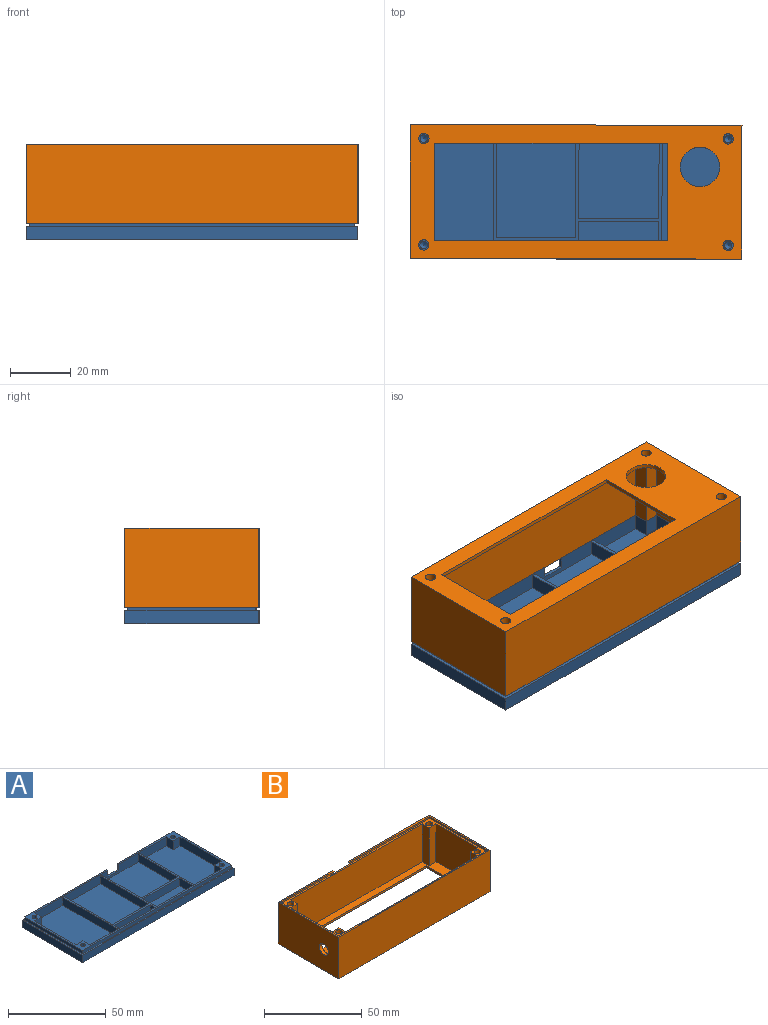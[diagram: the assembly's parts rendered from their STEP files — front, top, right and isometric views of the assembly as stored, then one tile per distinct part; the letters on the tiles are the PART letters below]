
ASSEMBLY  parts=2 mates=1
PART A: 58 faces, bbox 109x44x6.5 mm
  f0: plane 107x5mm, normal (0,1,0), area 218.5mm2, adj f27,f28,f30,f31,f40,f41,f50,f55
  f1: plane 35x26mm, normal (0,0,1), area 910mm2, adj f19,f20,f21,f25
  f2: plane 28.75x26.3mm, normal (0,0,1), area 756.1mm2, adj f16,f17,f18,f25
  f3: plane 40x24.2mm, normal (0,0,1), area 919.2mm2, adj f15,f24,f25,f26,f32,f33,f34,f35
  f4: plane 26.3x10.25mm, normal (0,0,1), area 269.6mm2, adj f12,f13,f14,f26
  f5: plane 26x4mm, normal (0,0,1), area 104mm2, adj f9,f10,f11,f26
  f6: plane 40x25.5mm, normal (0,0,1), area 970mm2, adj f8,f23,f25,f26,f36,f37,f38,f39
  f7: plane 109x44mm, normal (0,0,-1), area 4796mm2, adj f51,f52,f53,f54
  f8: plane 40x5mm, normal (-1,0,0), area 200mm2, adj f6,f22,f25,f26
  f9: plane 5x4mm, normal (1,0,0), area 20mm2, adj f5,f10,f22,f26
  f10: plane 26x5mm, normal (0,-1,0), area 130mm2, adj f5,f9,f11,f22
  f11: plane 5x4mm, normal (-1,0,0), area 20mm2, adj f5,f10,f22,f26
  f12: plane 10.25x5mm, normal (1,0,0), area 51.3mm2, adj f4,f13,f22,f26
  f13: plane 26.3x5mm, normal (0,-1,0), area 131.5mm2, adj f4,f12,f14,f22
  f14: plane 10.25x5mm, normal (-1,0,0), area 51.3mm2, adj f4,f13,f22,f26
  f15: plane 40x5mm, normal (1,0,0), area 200mm2, adj f3,f22,f25,f26
  f16: plane 28.75x5mm, normal (-1,0,0), area 143.8mm2, adj f2,f17,f22,f25
  f17: plane 26.3x5mm, normal (0,1,0), area 131.5mm2, adj f2,f16,f18,f22
  f18: plane 28.75x5mm, normal (1,0,0), area 143.8mm2, adj f2,f17,f22,f25
  f19: plane 35x5mm, normal (-1,0,0), area 175mm2, adj f1,f20,f22,f25
  f20: plane 26x5mm, normal (0,1,0), area 130mm2, adj f1,f19,f21,f22
  f21: plane 35x5mm, normal (1,0,0), area 175mm2, adj f1,f20,f22,f25
  f22: plane 55.3x40mm, normal (0,0,1), area 172.3mm2, adj f8,f9,f10,f11,f12,f13,f14,f15
  f23: plane 30x5.5mm, normal (1,0,0), area 165mm2, adj f6,f37,f38,f40
  f24: plane 30x5.5mm, normal (-1,0,0), area 165mm2, adj f3,f33,f34,f40
  f25: plane 95.12x5.5mm, normal (0,-1,0), area 478.1mm2, adj f1,f2,f3,f6,f8,f15,f16,f18
  f26: plane 95.12x5.5mm, normal (0,1,0), area 508.1mm2, adj f3,f4,f5,f6,f8,f9,f11,f12
  f27: plane 3.9x1mm, normal (1,0,0), area 3.9mm2, adj f0,f25,f40,f41
  f28: plane 42x2mm, normal (-1,0,0), area 84mm2, adj f0,f29,f40,f56
  f29: plane 107x2mm, normal (0,-1,0), area 214mm2, adj f28,f30,f40,f56
  f30: plane 42x2mm, normal (1,0,0), area 84mm2, adj f0,f29,f40,f56
  f31: plane 3.9x1mm, normal (-1,0,0), area 3.9mm2, adj f0,f25,f40,f41
  f32: plane 5.5x5mm, normal (-1,0,0), area 27.5mm2, adj f3,f25,f33,f40
  f33: plane 5.5x4.88mm, normal (0,-1,0), area 26.9mm2, adj f3,f24,f32,f40
  f34: plane 5.5x4.88mm, normal (0,1,0), area 26.9mm2, adj f3,f24,f35,f40
  f35: plane 5.5x5mm, normal (-1,0,0), area 27.5mm2, adj f3,f26,f34,f40
  f36: plane 5.5x5mm, normal (1,0,0), area 27.5mm2, adj f6,f26,f37,f40
  f37: plane 5.5x5mm, normal (0,1,0), area 27.5mm2, adj f6,f23,f36,f40
  f38: plane 5.5x5mm, normal (0,-1,0), area 27.5mm2, adj f6,f23,f39,f40
  f39: plane 5.5x5mm, normal (1,0,0), area 27.5mm2, adj f6,f25,f38,f40
  f40: plane 107x42mm, normal (0,0,1), area 365.5mm2, adj f0,f23,f24,f25,f26,f27,f28,f29
  f41: plane 7.7x1mm, normal (0,0,1), area 7.7mm2, adj f0,f25,f27,f31
  f42: cone r=0mm half-angle=59deg, axis (0,0,1), area 5.7mm2, adj f43
  f43: cylinder r=1.25mm len=4mm, axis (0,0,1), area 31.4mm2, adj f40,f42
  f44: cone r=0mm half-angle=59deg, axis (0,0,1), area 5.7mm2, adj f45
  f45: cylinder r=1.25mm len=4mm, axis (0,0,1), area 31.4mm2, adj f40,f44
  f46: cone r=0mm half-angle=59deg, axis (0,0,1), area 5.7mm2, adj f47
  f47: cylinder r=1.25mm len=4mm, axis (0,0,1), area 31.4mm2, adj f40,f46
  f48: cone r=0mm half-angle=59deg, axis (0,0,1), area 5.7mm2, adj f49
  f49: cylinder r=1.25mm len=4mm, axis (0,0,1), area 31.4mm2, adj f40,f48
  f50: plane 3x1mm, normal (1,0,0), area 3mm2, adj f0,f51,f56,f57
  f51: plane 109x4.5mm, normal (0,1,0), area 456mm2, adj f7,f50,f52,f54,f55,f56,f57
  f52: plane 44x4.5mm, normal (-1,0,0), area 198mm2, adj f7,f51,f53,f56
  f53: plane 109x4.5mm, normal (0,-1,0), area 490.5mm2, adj f7,f52,f54,f56
  f54: plane 44x4.5mm, normal (1,0,0), area 198mm2, adj f7,f51,f53,f56
  f55: plane 3x1mm, normal (-1,0,0), area 3mm2, adj f0,f51,f56,f57
  f56: plane 109x44mm, normal (0,0,1), area 290.5mm2, adj f0,f28,f29,f30,f50,f51,f52,f53
  f57: plane 11.5x1mm, normal (0,0,1), area 11.5mm2, adj f0,f50,f51,f55
PART B: 39 faces, bbox 109x44x26 mm
  f0: plane 11.5x1.5mm, normal (0,1,0), area 17.3mm2, adj f20,f26,f30,f31
  f1: plane 76.5x1.25mm, normal (0,1,0), area 95.6mm2, adj f2,f4,f5,f6
  f2: plane 32x1.25mm, normal (1,0,0), area 40mm2, adj f1,f3,f5,f6
  f3: plane 76.5x1.25mm, normal (0,-1,0), area 95.6mm2, adj f2,f4,f5,f6
  f4: plane 32x1.25mm, normal (-1,0,0), area 40mm2, adj f1,f3,f5,f6
  f5: plane 105x40mm, normal (0,0,1), area 1520.4mm2, adj f1,f2,f3,f4,f7,f8,f9,f10
  f6: plane 109x44mm, normal (0,0,-1), area 2179mm2, adj f1,f2,f3,f4,f7,f21,f22,f23
  f7: cylinder r=6.5mm len=13mm, axis (0,0,-1), area 51.1mm2, adj f5,f6
  f8: plane 95.12x23.75mm, normal (0,1,0), area 2259.1mm2, adj f5,f12,f19,f20
  f9: plane 30x23.75mm, normal (-1,0,0), area 712.5mm2, adj f5,f17,f18,f20
  f10: plane 95.12x23.75mm, normal (0,-1,0), area 2259.1mm2, adj f5,f15,f16,f20
  f11: plane 30x23.75mm, normal (1,0,0), area 679.3mm2, adj f5,f13,f14,f20,f38
  f12: plane 23.75x5mm, normal (1,0,0), area 118.8mm2, adj f5,f8,f13,f20
  f13: plane 23.75x5mm, normal (0,1,0), area 118.7mm2, adj f5,f11,f12,f20
  f14: plane 23.75x5mm, normal (0,-1,0), area 118.7mm2, adj f5,f11,f15,f20
  f15: plane 23.75x5mm, normal (1,0,0), area 118.8mm2, adj f5,f10,f14,f20
  f16: plane 23.75x5mm, normal (-1,0,0), area 118.8mm2, adj f5,f10,f17,f20
  f17: plane 23.75x4.88mm, normal (0,-1,0), area 115.9mm2, adj f5,f9,f16,f20
  f18: plane 23.75x4.88mm, normal (0,1,0), area 115.9mm2, adj f5,f9,f19,f20
  f19: plane 23.75x5mm, normal (-1,0,0), area 118.8mm2, adj f5,f8,f18,f20
  f20: plane 107x42mm, normal (0,0,1), area 356.5mm2, adj f0,f8,f9,f10,f11,f12,f13,f14
  f21: cylinder r=1.7mm len=25mm, axis (0,0,1), area 267mm2, adj f6,f20
  f22: cylinder r=1.7mm len=25mm, axis (0,0,1), area 267mm2, adj f6,f20
  f23: cylinder r=1.7mm len=25mm, axis (0,0,1), area 267mm2, adj f6,f20
  f24: cylinder r=1.7mm len=25mm, axis (0,0,1), area 267mm2, adj f6,f20
  f25: plane 109x26mm, normal (0,1,0), area 2805.2mm2, adj f6,f26,f30,f31,f34,f36,f37
  f26: plane 11.5x1mm, normal (0,0,1), area 11.5mm2, adj f0,f25,f30,f31
  f27: plane 42x1mm, normal (1,0,0), area 42mm2, adj f20,f28,f33,f37
  f28: plane 107x1mm, normal (0,1,0), area 107mm2, adj f20,f27,f29,f37
  f29: plane 42x1mm, normal (-1,0,0), area 42mm2, adj f20,f28,f32,f37
  f30: plane 2.5x1mm, normal (-1,0,0), area 2.5mm2, adj f0,f25,f26,f32,f37
  f31: plane 2.5x1mm, normal (1,0,0), area 2.5mm2, adj f0,f25,f26,f33,f37
  f32: plane 57.07x1mm, normal (0,-1,0), area 57.1mm2, adj f20,f29,f30,f37
  f33: plane 38.43x1mm, normal (0,-1,0), area 38.4mm2, adj f20,f27,f31,f37
  f34: plane 44x26mm, normal (-1,0,0), area 1110.8mm2, adj f6,f25,f35,f37,f38
  f35: plane 109x26mm, normal (0,-1,0), area 2834mm2, adj f6,f34,f36,f37
  f36: plane 44x26mm, normal (1,0,0), area 1144mm2, adj f6,f25,f35,f37
  f37: plane 109x44mm, normal (0,0,1), area 290.5mm2, adj f25,f27,f28,f29,f30,f31,f32,f33
  f38: cylinder r=3.25mm len=6.5mm, axis (-1,0,0), area 40.8mm2, adj f11,f34
PLACE A rot(axis=(0,0,-1),0.1deg) t=(-43.59,110.38,-21.92)mm
PLACE B rot(axis=(0,-1,0),180deg) t=(-43.55,110.39,9.58)mm
MATE fastened A.f46 <-> B.f22  axis (0,0,1) through (6.45,92.82,-15.42)mm
